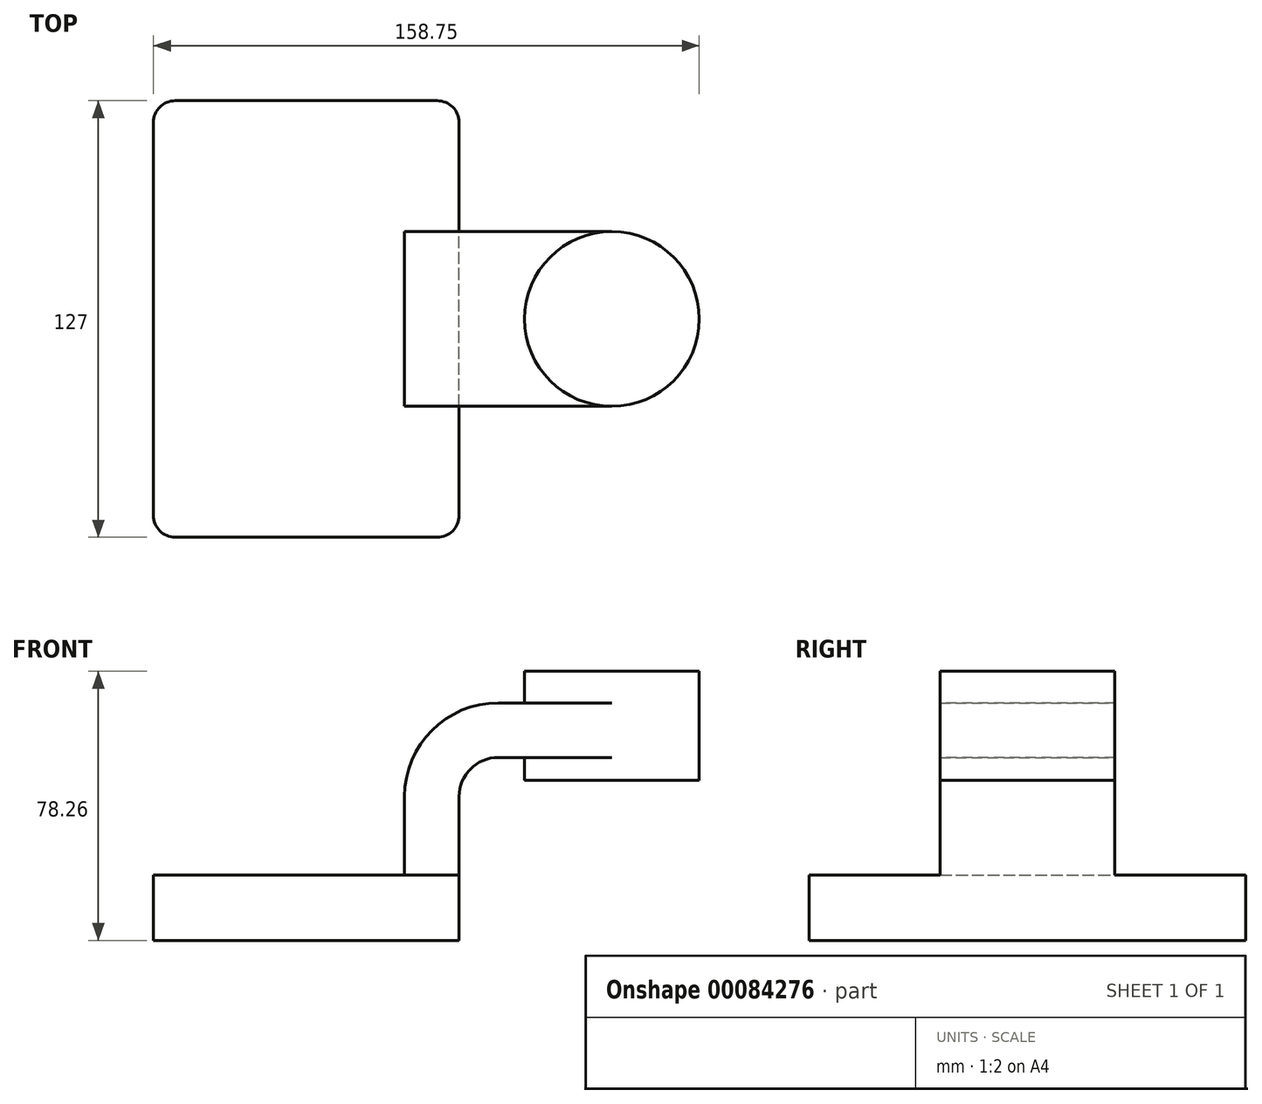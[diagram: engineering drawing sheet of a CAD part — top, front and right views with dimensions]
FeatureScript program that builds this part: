
annotation { "Feature Type Name" : "Feature", "Feature Type Description" : "" }
export const myFeature = defineFeature(function(context is Context, id is Id, definition is map)
    precondition{}
    {
        {
            var Q0;
            Q0=qCreatedBy(makeId("Front.planeOp"),FACE);
            var sketch = newSketch(context, id + "F0", { "sketchPlane" : qUnion([Q0])});
            skLineSegment(sketch, "E0.bottom", {"start": v(44.45, -9.52) * mm, "end": v(-44.45, -9.52) * mm});
            skLineSegment(sketch, "E0.top", {"start": v(44.45, 9.53) * mm, "end": v(-44.45, 9.53) * mm});
            skLineSegment(sketch, "E0.left", {"start": v(44.45, -9.52) * mm, "end": v(44.45, 9.53) * mm});
            skLineSegment(sketch, "E0.right", {"start": v(-44.45, -9.52) * mm, "end": v(-44.45, 9.53) * mm});
            skPoint(sketch, "E0.middle", {"position": v(0, 0) * mm});
            skLineSegment(sketch, "E1.bottom", {"start": v(114.3, 36.98) * mm, "end": v(63.5, 36.98) * mm});
            skLineSegment(sketch, "E1.top", {"start": v(114.3, 68.73) * mm, "end": v(63.5, 68.73) * mm});
            skLineSegment(sketch, "E1.left", {"start": v(114.3, 36.98) * mm, "end": v(114.3, 68.73) * mm});
            skLineSegment(sketch, "E1.right", {"start": v(63.5, 36.98) * mm, "end": v(63.5, 68.73) * mm});
            skPoint(sketch, "E1.middle", {"position": v(88.9, 52.86) * mm});
            skLineSegment(sketch, "E2", {"start": v(44.45, 9.53) * mm, "end": v(44.45, 32.28) * mm});
            skArc(sketch, "E3", {"start": v(44.45, 32.28) * mm, "mid": v(47.79, 40.34) * mm, "end": v(55.85, 43.68) * mm});
            skLineSegment(sketch, "E4", {"start": v(55.85, 43.68) * mm, "end": v(88.9, 43.68) * mm});
            skLineSegment(sketch, "E5.0", {"start": v(55.85, 59.56) * mm, "end": v(88.9, 59.56) * mm});
            skArc(sketch, "E5.1", {"start": v(28.57, 32.28) * mm, "mid": v(36.56, 51.57) * mm, "end": v(55.85, 59.56) * mm});
            skLineSegment(sketch, "E5.2", {"start": v(28.57, 9.53) * mm, "end": v(28.57, 32.28) * mm});
            skLineSegment(sketch, "E6", {"start": v(88.9, 68.73) * mm, "end": v(88.9, 36.98) * mm});
            skFitSpline(sketch, "E7", {"points": [v(-44.45, 9.53) * mm, v(0, 20.52) * mm, v(63.5, 59.56) * mm], "startDerivative": vector(16.05, 27.35) * mm, "endDerivative": vector(402.5, -20.66) * mm});
            skSolve(sketch);
        }
        {
            var Q0;
            Q0=makeQuery(id+"F0.imprint","IMPRINT",FACE,{"disambiguationData":[TD([[makeQuery(id+"F0.imprint","IMPRINT",EDGE,{"derivedFrom":sQuery(id+"F0.wireOp",EDGE,"E0.bottom")}),-1.0]])]});
            extrude(context, id + "F1", {"entities" : qUnion([Q0]), "endBound" : BoundingType.SYMMETRIC, "depth" : 127 * mm});
        }
        {
            var Q0;
            {var subQ1=sQuery(id+"F0.wireOp",EDGE,"E2");Q0=makeQuery(id+"F0.imprint","IMPRINT",FACE,{"disambiguationData":[TD([[makeQuery(id+"F0.imprint","IMPRINT",EDGE,{"derivedFrom":subQ1}),1.0]])]});}
            var Q1;
            {var subQ3=sQuery(id+"F0.wireOp",EDGE,"E4");var subQ5=sQuery(id+"F0.wireOp",EDGE,"E6");var subQ6=makeQuery(id+"F0.imprint","INTERSECT",VERTEX,{"derivedFrom":[subQ3,subQ5]});Q1=makeQuery(id+"F0.imprint","IMPRINT",FACE,{"disambiguationData":[TD([[makeQuery(id+"F0.imprint","IMPRINT",EDGE,{"disambiguationData":[TD([[subQ6,1.0]])],"derivedFrom":subQ3}),1.0]])]});}
            extrude(context, id + "F2", {"entities" : qUnion([Q0, Q1]), "operationType" : NewBodyOperationType.ADD, "endBound" : BoundingType.SYMMETRIC, "depth" : 50.8 * mm});
        }
        {
            var Q0;
            {var subQ1=sQuery(id+"F0.wireOp",EDGE,"E5.1");Q0=makeQuery(id+"F0.imprint","IMPRINT",FACE,{"disambiguationData":[TD([[makeQuery(id+"F0.imprint","IMPRINT",EDGE,{"derivedFrom":subQ1}),1.0]])]});}
            extrude(context, id + "F3", {"entities" : qUnion([Q0]), "operationType" : NewBodyOperationType.ADD, "endBound" : BoundingType.SYMMETRIC, "depth" : 19.05 * mm});
        }
        {
            var Q0;
            {var subQ0=sQuery(id+"F0.wireOp",EDGE,"E1.left");Q0=makeQuery(id+"F0.imprint","IMPRINT",FACE,{"disambiguationData":[TD([[makeQuery(id+"F0.imprint","IMPRINT",EDGE,{"derivedFrom":subQ0}),1.0]])]});}
            var Q1;
            Q1=sQuery(id+"F0.wireOp",EDGE,"E6");
            revolve(context, id + "F4", {"operationType" : NewBodyOperationType.ADD, "entities" : qUnion([Q0]), "axis" : qUnion([Q1]), "revolveType" : RevolveType.FULL});
        }
        {
            var Q0;
            Q0=makeQuery(id+"F1.opExtrude","CAP_EDGE",EDGE,{"disambiguationData":[OSD([sQuery(id+"F0.wireOp",EDGE,"E0.right")])],"isStart":false});
            var Q1;
            Q1=makeQuery(id+"F1.opExtrude","CAP_EDGE",EDGE,{"disambiguationData":[OSD([sQuery(id+"F0.wireOp",EDGE,"E0.left")])],"isStart":false});
            var Q2;
            Q2=makeQuery(id+"F1.opExtrude","CAP_EDGE",EDGE,{"disambiguationData":[OSD([sQuery(id+"F0.wireOp",EDGE,"E0.left")])],"isStart":true});
            var Q3;
            Q3=makeQuery(id+"F1.opExtrude","CAP_EDGE",EDGE,{"disambiguationData":[OSD([sQuery(id+"F0.wireOp",EDGE,"E0.right")])],"isStart":true});
            fillet(context, id + "F5", {"entities" : qUnion([Q0, Q1, Q2, Q3]), "radius" : 6.35 * mm, "tangentPropagation" : true, "allowEdgeOverflow" : false});
        }
    });
